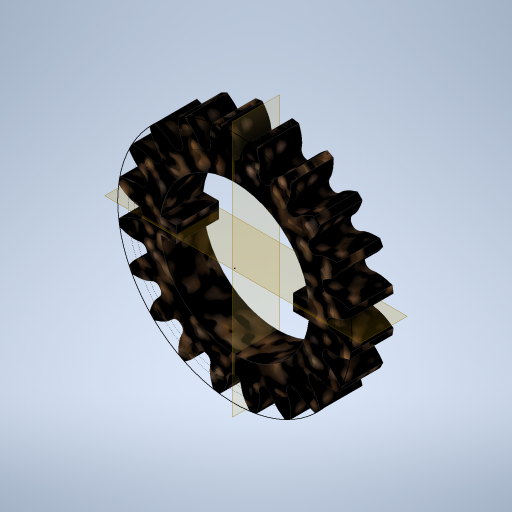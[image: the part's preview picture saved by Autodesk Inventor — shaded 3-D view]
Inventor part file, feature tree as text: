
AUTODESK INVENTOR PART (.ipt)
format: ipt  version: 2023 (Build 270158000, 158)  size: 460,288 bytes
history: native  units: mm
features: extrude x3, sketch x2, pattern_circular x1
ambient origin geometry x8: Origin, YZ Plane, XZ Plane, XY Plane, X Axis, Y Axis, Z Axis, Center Point
bodies: Solid1 (feature_tree)
feature tree (6):
  sketch  "Sketch1"  dims[d0=8.0mm d1=0.0mm]
  extrude  "Extrusion1"  TaperAngle=0.0deg  [1 undecoded]
  extrude  "Extrusion2"  Depth=10.0mm TaperAngle=360.0deg
  pattern_circular  "Circular Pattern1"  [2 undecoded]
  extrude  "Extrusion3"  Depth=3.0mm
  sketch  "Sketch2"  dims[d2=10.0mm d3=0.0mm d4=200.0mm d5=360.0deg d7=28.0mm d8=3.0mm d10=6.0mm d11=10.0mm d12=0.0mm]
note: 3 required parameter values undecoded (feature->parameter linkage not recoverable at this tier; creation-order binding heuristic only, values carry confidence <= 0.55)
